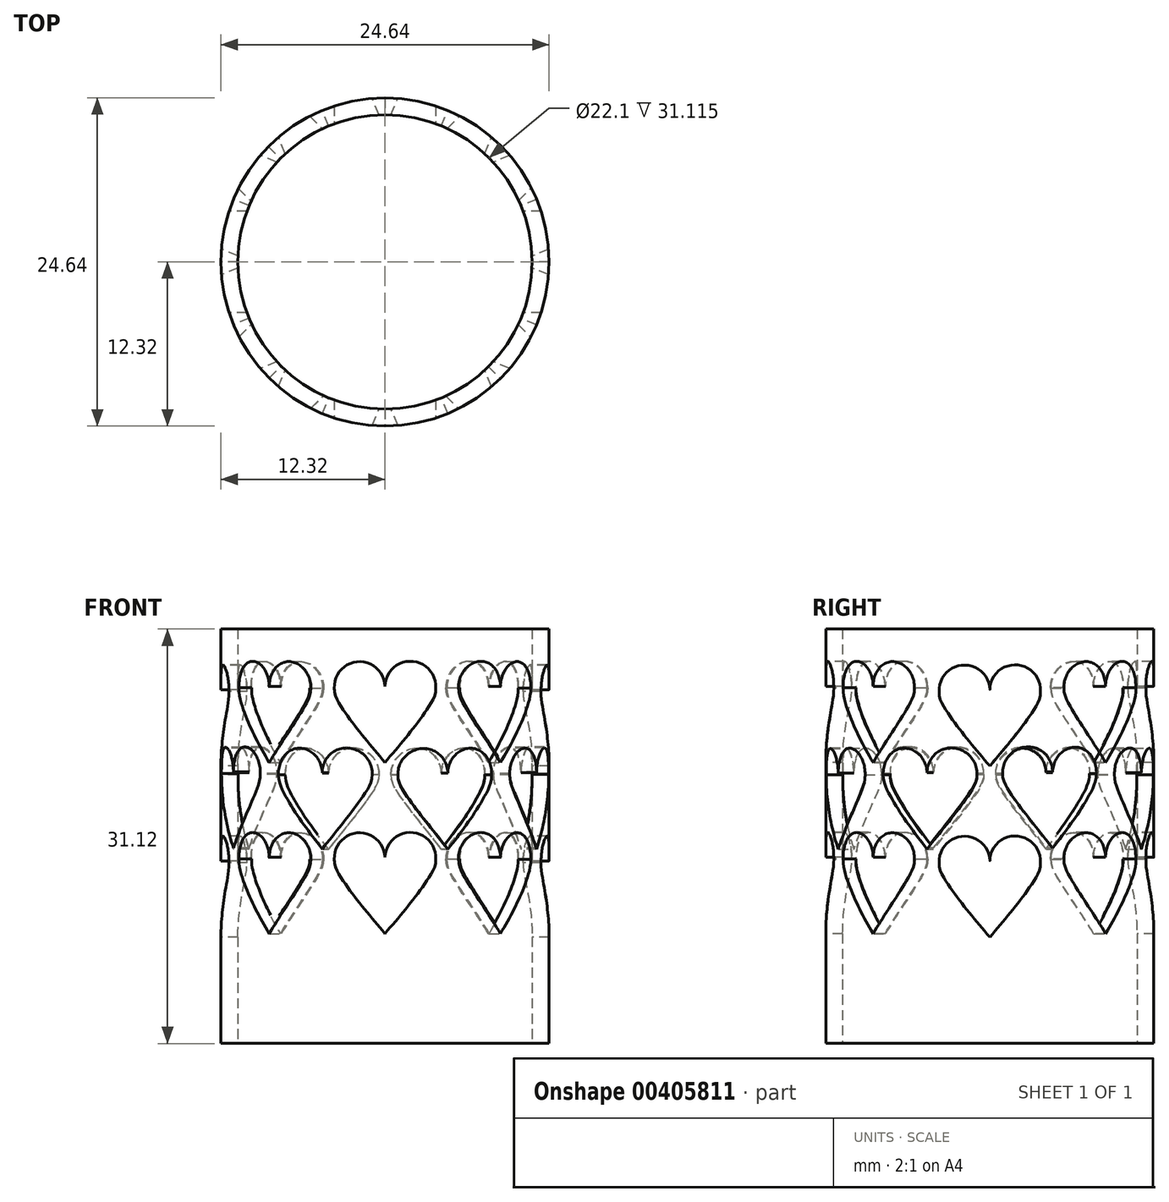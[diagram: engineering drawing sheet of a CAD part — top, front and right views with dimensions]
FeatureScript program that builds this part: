
annotation { "Feature Type Name" : "Feature", "Feature Type Description" : "" }
export const myFeature = defineFeature(function(context is Context, id is Id, definition is map)
    precondition{}
    {
        {
            var Q0;
            Q0=qCreatedBy(makeId("Top.planeOp"),FACE);
            var sketch = newSketch(context, id + "F0", { "sketchPlane" : qUnion([Q0])});
            skCircle(sketch, "E0", {"center": v(0, 0) * mm, "radius": 11.05 * mm});
            skCircle(sketch, "E1.0", {"center": v(0, 0) * mm, "radius": 12.32 * mm});
            skSolve(sketch);
        }
        {
            var Q0;
            Q0 = qSketchRegion(id + "F0", true);
            extrude(context, id + "F1", {"entities" : qUnion([Q0]), "depth" : 25.4 * mm, "hasSecondDirection" : true, "secondDirectionOppositeDirection" : true, "secondDirectionDepth" : 5.7 * mm});
        }
        {
            var Q0;
            Q0=qCreatedBy(makeId("Front.planeOp"),FACE);
            var sketch = newSketch(context, id + "F2", { "sketchPlane" : qUnion([Q0])});
            skLineSegment(sketch, "E2", {"start": v(-15.94, 0) * mm, "end": v(15.78, 0) * mm, "construction": true});
            skFitSpline(sketch, "E3.0", {"points": [v(-3.81, 8.23) * mm, v(-3.8, 8.14) * mm, v(-3.8, 8) * mm, v(-3.8, 7.85) * mm, v(-3.77, 7.7) * mm, v(-3.72, 7.54) * mm, v(-3.63, 7.32) * mm, v(-3.45, 7) * mm, v(-3.2, 6.6) * mm, v(-2.8, 6) * mm, v(-2.14, 5.12) * mm, v(-1.2, 3.96) * mm, v(-0.14, 2.7) * mm, v(0.6, 1.84) * mm, v(0.97, 1.4) * mm]});
            skArc(sketch, "E4", {"start": v(0, 8.17) * mm, "mid": v(-1.94, 10.1) * mm, "end": v(-3.8, 8.1) * mm});
            skArc(sketch, "E5", {"start": v(3.8, 8.13) * mm, "mid": v(1.93, 10.13) * mm, "end": v(0, 8.17) * mm});
            skFitSpline(sketch, "E6.0", {"points": [v(3.81, 8.23) * mm, v(3.8, 8.14) * mm, v(3.8, 8) * mm, v(3.8, 7.85) * mm, v(3.77, 7.7) * mm, v(3.72, 7.54) * mm, v(3.63, 7.32) * mm, v(3.45, 7) * mm, v(3.2, 6.6) * mm, v(2.8, 6) * mm, v(2.14, 5.12) * mm, v(1.2, 3.96) * mm, v(0.14, 2.7) * mm, v(-0.6, 1.84) * mm, v(-0.97, 1.4) * mm]});
            skFitSpline(sketch, "E7.0", {"points": [v(-3.81, 21.08) * mm, v(-3.8, 21) * mm, v(-3.8, 20.85) * mm, v(-3.8, 20.7) * mm, v(-3.77, 20.56) * mm, v(-3.72, 20.4) * mm, v(-3.63, 20.17) * mm, v(-3.45, 19.84) * mm, v(-3.2, 19.45) * mm, v(-2.8, 18.85) * mm, v(-2.14, 17.98) * mm, v(-1.2, 16.8) * mm, v(-0.14, 15.56) * mm, v(0.6, 14.7) * mm, v(0.97, 14.26) * mm]});
            skArc(sketch, "E8", {"start": v(0, 21.02) * mm, "mid": v(-1.94, 22.96) * mm, "end": v(-3.8, 20.96) * mm});
            skArc(sketch, "E9", {"start": v(3.8, 20.98) * mm, "mid": v(1.93, 22.98) * mm, "end": v(0, 21.02) * mm});
            skFitSpline(sketch, "E10.0", {"points": [v(3.81, 21.08) * mm, v(3.8, 21) * mm, v(3.8, 20.85) * mm, v(3.8, 20.7) * mm, v(3.77, 20.56) * mm, v(3.72, 20.4) * mm, v(3.63, 20.17) * mm, v(3.45, 19.84) * mm, v(3.2, 19.45) * mm, v(2.8, 18.85) * mm, v(2.14, 17.98) * mm, v(1.2, 16.8) * mm, v(0.14, 15.56) * mm, v(-0.6, 14.7) * mm, v(-0.97, 14.26) * mm]});
            skSolve(sketch);
        }
        {
            var Q0;
            Q0 = qSketchRegion(id + "F2", true);
            extrude(context, id + "F3", {"entities" : qUnion([Q0]), "operationType" : NewBodyOperationType.REMOVE, "endBound" : BoundingType.SYMMETRIC, "oppositeDirection" : true, "depth" : 50.8 * mm});
        }
        {
            var Q0;
            Q0=qCreatedBy(makeId("Right.planeOp"),FACE);
            var sketch = newSketch(context, id + "F4", { "sketchPlane" : qUnion([Q0])});
            skLineSegment(sketch, "E11", {"start": v(-15.94, -0.26) * mm, "end": v(15.78, -0.26) * mm, "construction": true});
            skFitSpline(sketch, "E12.0", {"points": [v(-3.81, 7.96) * mm, v(-3.8, 7.88) * mm, v(-3.8, 7.74) * mm, v(-3.8, 7.58) * mm, v(-3.77, 7.45) * mm, v(-3.72, 7.28) * mm, v(-3.63, 7.05) * mm, v(-3.45, 6.73) * mm, v(-3.2, 6.33) * mm, v(-2.8, 5.73) * mm, v(-2.14, 4.86) * mm, v(-1.2, 3.7) * mm, v(-0.14, 2.44) * mm, v(0.6, 1.58) * mm, v(0.97, 1.15) * mm]});
            skArc(sketch, "E13", {"start": v(0, 7.9) * mm, "mid": v(-1.94, 9.85) * mm, "end": v(-3.8, 7.84) * mm});
            skArc(sketch, "E14", {"start": v(3.8, 7.86) * mm, "mid": v(1.93, 9.87) * mm, "end": v(0, 7.9) * mm});
            skFitSpline(sketch, "E15.0", {"points": [v(3.81, 7.96) * mm, v(3.8, 7.88) * mm, v(3.8, 7.74) * mm, v(3.8, 7.58) * mm, v(3.77, 7.45) * mm, v(3.72, 7.28) * mm, v(3.63, 7.05) * mm, v(3.45, 6.73) * mm, v(3.2, 6.33) * mm, v(2.8, 5.73) * mm, v(2.14, 4.86) * mm, v(1.2, 3.7) * mm, v(0.14, 2.44) * mm, v(-0.6, 1.58) * mm, v(-0.97, 1.15) * mm]});
            skFitSpline(sketch, "E16.0", {"points": [v(-3.81, 20.82) * mm, v(-3.8, 20.73) * mm, v(-3.8, 20.6) * mm, v(-3.8, 20.44) * mm, v(-3.77, 20.3) * mm, v(-3.72, 20.13) * mm, v(-3.63, 19.9) * mm, v(-3.45, 19.58) * mm, v(-3.2, 19.19) * mm, v(-2.8, 18.58) * mm, v(-2.14, 17.72) * mm, v(-1.2, 16.55) * mm, v(-0.14, 15.3) * mm, v(0.6, 14.43) * mm, v(0.97, 14) * mm]});
            skArc(sketch, "E17", {"start": v(0, 20.76) * mm, "mid": v(-1.94, 22.7) * mm, "end": v(-3.8, 20.7) * mm});
            skArc(sketch, "E18", {"start": v(3.8, 20.72) * mm, "mid": v(1.93, 22.72) * mm, "end": v(0, 20.76) * mm});
            skFitSpline(sketch, "E19.0", {"points": [v(3.81, 20.82) * mm, v(3.8, 20.73) * mm, v(3.8, 20.6) * mm, v(3.8, 20.44) * mm, v(3.77, 20.3) * mm, v(3.72, 20.13) * mm, v(3.63, 19.9) * mm, v(3.45, 19.58) * mm, v(3.2, 19.19) * mm, v(2.8, 18.58) * mm, v(2.14, 17.72) * mm, v(1.2, 16.55) * mm, v(0.14, 15.3) * mm, v(-0.6, 14.43) * mm, v(-0.97, 14) * mm]});
            skSolve(sketch);
        }
        {
            var Q0;
            Q0 = qSketchRegion(id + "F4", true);
            extrude(context, id + "F5", {"entities" : qUnion([Q0]), "operationType" : NewBodyOperationType.REMOVE, "endBound" : BoundingType.SYMMETRIC, "depth" : 50.8 * mm});
        }
        {
            var Q0;
            Q0=qCreatedBy(makeId("Top.planeOp"),FACE);
            var sketch = newSketch(context, id + "F6", { "sketchPlane" : qUnion([Q0])});
            skLineSegment(sketch, "E20", {"start": v(-35.33, -35.33) * mm, "end": v(35.33, 35.33) * mm, "construction": true});
            skLineSegment(sketch, "E21.MirrorCS", {"start": v(35.33, -35.33) * mm, "end": v(-35.33, 35.33) * mm, "construction": true});
            skLineSegment(sketch, "E22", {"start": v(0, 0) * mm, "end": v(25.2, 60.83) * mm, "construction": true});
            skLineSegment(sketch, "E23.1.0", {"start": v(0, 0) * mm, "end": v(-25.2, 60.83) * mm, "construction": true});
            skLineSegment(sketch, "E23.2.0", {"start": v(0, 0) * mm, "end": v(-60.83, 25.2) * mm, "construction": true});
            skLineSegment(sketch, "E23.3.0", {"start": v(0, 0) * mm, "end": v(-60.83, -25.2) * mm, "construction": true});
            skLineSegment(sketch, "E23.4.0", {"start": v(0, 0) * mm, "end": v(-25.2, -60.83) * mm, "construction": true});
            skLineSegment(sketch, "E23.5.0", {"start": v(0, 0) * mm, "end": v(25.2, -60.83) * mm, "construction": true});
            skLineSegment(sketch, "E23.6.0", {"start": v(0, 0) * mm, "end": v(60.83, -25.2) * mm, "construction": true});
            skLineSegment(sketch, "E23.7.0", {"start": v(0, 0) * mm, "end": v(60.83, 25.2) * mm, "construction": true});
            skPoint(sketch, "E23.center", {"position": v(0, 0) * mm});
            skSolve(sketch);
        }
        {
            var Q0;
            Q0=sQuery(id+"F6.wireOp",EDGE,"E21.MirrorCS");
            cPlane(context, id + "F7", {"entities" : qUnion([Q0]), "cplaneType" : CPlaneType.MID_PLANE, "offset" : 25.4 * mm, "width" : 152.4 * mm, "height" : 152.4 * mm});
        }
        {
            var Q0;
            Q0=sQuery(id+"F6.wireOp",EDGE,"E20");
            cPlane(context, id + "F8", {"entities" : qUnion([Q0]), "cplaneType" : CPlaneType.MID_PLANE, "offset" : 25.4 * mm, "width" : 152.4 * mm, "height" : 152.4 * mm});
        }
        {
            var Q0;
            Q0=qCreatedBy(id+"F7.planeOp",FACE);
            var sketch = newSketch(context, id + "F9", { "sketchPlane" : qUnion([Q0])});
            skLineSegment(sketch, "E24", {"start": v(-15.87, 0) * mm, "end": v(15.85, 0) * mm, "construction": true});
            skFitSpline(sketch, "E25.0", {"points": [v(-3.74, 8.23) * mm, v(-3.74, 8.14) * mm, v(-3.73, 8) * mm, v(-3.72, 7.85) * mm, v(-3.7, 7.7) * mm, v(-3.65, 7.54) * mm, v(-3.56, 7.32) * mm, v(-3.38, 7) * mm, v(-3.13, 6.6) * mm, v(-2.72, 6) * mm, v(-2.07, 5.12) * mm, v(-1.12, 3.96) * mm, v(-0.07, 2.7) * mm, v(0.67, 1.84) * mm, v(1.04, 1.4) * mm]});
            skArc(sketch, "E26", {"start": v(0.07, 8.17) * mm, "mid": v(-1.86, 10.1) * mm, "end": v(-3.74, 8.1) * mm});
            skArc(sketch, "E27", {"start": v(3.88, 8.13) * mm, "mid": v(2, 10.13) * mm, "end": v(0.07, 8.17) * mm});
            skFitSpline(sketch, "E28.0", {"points": [v(3.88, 8.23) * mm, v(3.88, 8.14) * mm, v(3.88, 8) * mm, v(3.87, 7.85) * mm, v(3.84, 7.7) * mm, v(3.8, 7.54) * mm, v(3.7, 7.32) * mm, v(3.52, 7) * mm, v(3.28, 6.6) * mm, v(2.87, 6) * mm, v(2.21, 5.12) * mm, v(1.27, 3.96) * mm, v(0.22, 2.7) * mm, v(-0.52, 1.84) * mm, v(-0.9, 1.4) * mm]});
            skFitSpline(sketch, "E29.0", {"points": [v(-3.74, 21.08) * mm, v(-3.74, 21) * mm, v(-3.73, 20.85) * mm, v(-3.72, 20.7) * mm, v(-3.7, 20.56) * mm, v(-3.65, 20.4) * mm, v(-3.56, 20.17) * mm, v(-3.38, 19.84) * mm, v(-3.13, 19.45) * mm, v(-2.72, 18.85) * mm, v(-2.07, 17.98) * mm, v(-1.12, 16.8) * mm, v(-0.07, 15.56) * mm, v(0.67, 14.7) * mm, v(1.04, 14.26) * mm]});
            skArc(sketch, "E30", {"start": v(0.07, 21.02) * mm, "mid": v(-1.86, 22.96) * mm, "end": v(-3.74, 20.96) * mm});
            skArc(sketch, "E31", {"start": v(3.88, 20.98) * mm, "mid": v(2, 22.98) * mm, "end": v(0.07, 21.02) * mm});
            skFitSpline(sketch, "E32.0", {"points": [v(3.88, 21.08) * mm, v(3.88, 21) * mm, v(3.88, 20.85) * mm, v(3.87, 20.7) * mm, v(3.84, 20.56) * mm, v(3.8, 20.4) * mm, v(3.7, 20.17) * mm, v(3.52, 19.84) * mm, v(3.28, 19.45) * mm, v(2.87, 18.85) * mm, v(2.21, 17.98) * mm, v(1.27, 16.8) * mm, v(0.22, 15.56) * mm, v(-0.52, 14.7) * mm, v(-0.9, 14.26) * mm]});
            skSolve(sketch);
        }
        {
            var Q0;
            Q0 = qSketchRegion(id + "F9", true);
            extrude(context, id + "F10", {"entities" : qUnion([Q0]), "operationType" : NewBodyOperationType.REMOVE, "endBound" : BoundingType.SYMMETRIC, "depth" : 50.8 * mm});
        }
        {
            var Q0;
            Q0=qCreatedBy(id+"F8.planeOp",FACE);
            var sketch = newSketch(context, id + "F11", { "sketchPlane" : qUnion([Q0])});
            skLineSegment(sketch, "E33", {"start": v(-15.96, 0) * mm, "end": v(15.75, 0) * mm, "construction": true});
            skFitSpline(sketch, "E34.0", {"points": [v(-3.83, 8.23) * mm, v(-3.83, 8.14) * mm, v(-3.83, 8) * mm, v(-3.82, 7.85) * mm, v(-3.8, 7.7) * mm, v(-3.75, 7.54) * mm, v(-3.65, 7.32) * mm, v(-3.48, 7) * mm, v(-3.23, 6.6) * mm, v(-2.82, 6) * mm, v(-2.16, 5.12) * mm, v(-1.22, 3.96) * mm, v(-0.17, 2.7) * mm, v(0.57, 1.84) * mm, v(0.94, 1.4) * mm]});
            skArc(sketch, "E35", {"start": v(-0.02, 8.17) * mm, "mid": v(-1.96, 10.1) * mm, "end": v(-3.83, 8.1) * mm});
            skArc(sketch, "E36", {"start": v(3.78, 8.13) * mm, "mid": v(1.9, 10.13) * mm, "end": v(-0.02, 8.17) * mm});
            skFitSpline(sketch, "E37.0", {"points": [v(3.79, 8.23) * mm, v(3.78, 8.14) * mm, v(3.78, 8) * mm, v(3.77, 7.85) * mm, v(3.75, 7.7) * mm, v(3.7, 7.54) * mm, v(3.6, 7.32) * mm, v(3.43, 7) * mm, v(3.18, 6.6) * mm, v(2.77, 6) * mm, v(2.12, 5.12) * mm, v(1.17, 3.96) * mm, v(0.12, 2.7) * mm, v(-0.62, 1.84) * mm, v(-0.99, 1.4) * mm]});
            skFitSpline(sketch, "E38.0", {"points": [v(-3.83, 21.08) * mm, v(-3.83, 21) * mm, v(-3.83, 20.85) * mm, v(-3.82, 20.7) * mm, v(-3.8, 20.56) * mm, v(-3.75, 20.4) * mm, v(-3.65, 20.17) * mm, v(-3.48, 19.84) * mm, v(-3.23, 19.45) * mm, v(-2.82, 18.85) * mm, v(-2.16, 17.98) * mm, v(-1.22, 16.8) * mm, v(-0.17, 15.56) * mm, v(0.57, 14.7) * mm, v(0.94, 14.26) * mm]});
            skArc(sketch, "E39", {"start": v(-0.02, 21.02) * mm, "mid": v(-1.96, 22.96) * mm, "end": v(-3.83, 20.96) * mm});
            skArc(sketch, "E40", {"start": v(3.78, 20.98) * mm, "mid": v(1.9, 22.98) * mm, "end": v(-0.02, 21.02) * mm});
            skFitSpline(sketch, "E41.0", {"points": [v(3.79, 21.08) * mm, v(3.78, 21) * mm, v(3.78, 20.85) * mm, v(3.77, 20.7) * mm, v(3.75, 20.56) * mm, v(3.7, 20.4) * mm, v(3.6, 20.17) * mm, v(3.43, 19.84) * mm, v(3.18, 19.45) * mm, v(2.77, 18.85) * mm, v(2.12, 17.98) * mm, v(1.17, 16.8) * mm, v(0.12, 15.56) * mm, v(-0.62, 14.7) * mm, v(-0.99, 14.26) * mm]});
            skSolve(sketch);
        }
        {
            var Q0;
            Q0 = qSketchRegion(id + "F11", true);
            extrude(context, id + "F12", {"entities" : qUnion([Q0]), "operationType" : NewBodyOperationType.REMOVE, "endBound" : BoundingType.SYMMETRIC, "oppositeDirection" : true, "depth" : 50.8 * mm});
        }
        {
            var Q0;
            Q0=sQuery(id+"F6.wireOp",VERTEX,"E23.2.0.end");
            var Q1;
            Q1=sQuery(id+"F6.wireOp",VERTEX,"E23.6.0.end");
            cPlane(context, id + "F13", {"entities" : qUnion([Q0, Q1]), "cplaneType" : CPlaneType.MID_PLANE, "offset" : 25.4 * mm, "width" : 152.4 * mm, "height" : 152.4 * mm});
        }
        {
            var Q0;
            Q0=qCreatedBy(id+"F13.planeOp",FACE);
            var sketch = newSketch(context, id + "F14", { "sketchPlane" : qUnion([Q0])});
            skFitSpline(sketch, "E42.0", {"points": [v(-3.81, 14.58) * mm, v(-3.8, 14.5) * mm, v(-3.8, 14.35) * mm, v(-3.8, 14.2) * mm, v(-3.77, 14.06) * mm, v(-3.72, 13.9) * mm, v(-3.63, 13.67) * mm, v(-3.45, 13.34) * mm, v(-3.2, 12.95) * mm, v(-2.8, 12.34) * mm, v(-2.14, 11.47) * mm, v(-1.2, 10.3) * mm, v(-0.14, 9.06) * mm, v(0.6, 8.2) * mm, v(0.97, 7.76) * mm]});
            skArc(sketch, "E43", {"start": v(0, 14.52) * mm, "mid": v(-1.94, 16.46) * mm, "end": v(-3.8, 14.45) * mm});
            skArc(sketch, "E44", {"start": v(3.8, 14.48) * mm, "mid": v(1.93, 16.48) * mm, "end": v(0, 14.52) * mm});
            skFitSpline(sketch, "E45.0", {"points": [v(3.81, 14.58) * mm, v(3.8, 14.5) * mm, v(3.8, 14.35) * mm, v(3.8, 14.2) * mm, v(3.77, 14.06) * mm, v(3.72, 13.9) * mm, v(3.63, 13.67) * mm, v(3.45, 13.34) * mm, v(3.2, 12.95) * mm, v(2.8, 12.34) * mm, v(2.14, 11.47) * mm, v(1.2, 10.3) * mm, v(0.14, 9.06) * mm, v(-0.6, 8.2) * mm, v(-0.97, 7.76) * mm]});
            skSolve(sketch);
        }
        {
            var Q0;
            Q0 = qSketchRegion(id + "F14", true);
            extrude(context, id + "F15", {"entities" : qUnion([Q0]), "operationType" : NewBodyOperationType.REMOVE, "endBound" : BoundingType.SYMMETRIC, "depth" : 50.8 * mm});
        }
        {
            var Q0;
            Q0=sQuery(id+"F6.wireOp",VERTEX,"E23.1.0.end");
            var Q1;
            Q1=sQuery(id+"F6.wireOp",VERTEX,"E23.5.0.end");
            cPlane(context, id + "F16", {"entities" : qUnion([Q0, Q1]), "cplaneType" : CPlaneType.MID_PLANE, "offset" : 25.4 * mm, "width" : 152.4 * mm, "height" : 152.4 * mm});
        }
        {
            var Q0;
            Q0=qCreatedBy(id+"F16.planeOp",FACE);
            var sketch = newSketch(context, id + "F17", { "sketchPlane" : qUnion([Q0])});
            skFitSpline(sketch, "E46.0", {"points": [v(-3.81, 14.55) * mm, v(-3.8, 14.47) * mm, v(-3.8, 14.33) * mm, v(-3.8, 14.17) * mm, v(-3.77, 14.03) * mm, v(-3.72, 13.87) * mm, v(-3.63, 13.64) * mm, v(-3.45, 13.32) * mm, v(-3.2, 12.92) * mm, v(-2.8, 12.32) * mm, v(-2.14, 11.45) * mm, v(-1.2, 10.28) * mm, v(-0.14, 9.03) * mm, v(0.6, 8.17) * mm, v(0.97, 7.73) * mm]});
            skArc(sketch, "E47", {"start": v(0, 14.5) * mm, "mid": v(-1.94, 16.43) * mm, "end": v(-3.8, 14.43) * mm});
            skArc(sketch, "E48", {"start": v(3.8, 14.45) * mm, "mid": v(1.93, 16.46) * mm, "end": v(0, 14.5) * mm});
            skFitSpline(sketch, "E49.0", {"points": [v(3.81, 14.55) * mm, v(3.8, 14.47) * mm, v(3.8, 14.33) * mm, v(3.8, 14.17) * mm, v(3.77, 14.03) * mm, v(3.72, 13.87) * mm, v(3.63, 13.64) * mm, v(3.45, 13.32) * mm, v(3.2, 12.92) * mm, v(2.8, 12.32) * mm, v(2.14, 11.45) * mm, v(1.2, 10.28) * mm, v(0.14, 9.03) * mm, v(-0.6, 8.17) * mm, v(-0.97, 7.73) * mm]});
            skSolve(sketch);
        }
        {
            var Q0;
            Q0 = qSketchRegion(id + "F17", true);
            extrude(context, id + "F18", {"entities" : qUnion([Q0]), "operationType" : NewBodyOperationType.REMOVE, "endBound" : BoundingType.SYMMETRIC, "depth" : 50.8 * mm});
        }
        {
            var Q0;
            Q0=sQuery(id+"F6.wireOp",VERTEX,"E22.end");
            var Q1;
            Q1=sQuery(id+"F6.wireOp",VERTEX,"E23.4.0.end");
            cPlane(context, id + "F19", {"entities" : qUnion([Q0, Q1]), "cplaneType" : CPlaneType.MID_PLANE, "offset" : 25.4 * mm, "width" : 152.4 * mm, "height" : 152.4 * mm});
        }
        {
            var Q0;
            Q0=qCreatedBy(id+"F19.planeOp",FACE);
            var sketch = newSketch(context, id + "F20", { "sketchPlane" : qUnion([Q0])});
            skFitSpline(sketch, "E50.0", {"points": [v(-3.81, 14.58) * mm, v(-3.8, 14.5) * mm, v(-3.8, 14.35) * mm, v(-3.8, 14.2) * mm, v(-3.77, 14.06) * mm, v(-3.72, 13.9) * mm, v(-3.63, 13.67) * mm, v(-3.45, 13.34) * mm, v(-3.2, 12.95) * mm, v(-2.8, 12.34) * mm, v(-2.14, 11.47) * mm, v(-1.2, 10.3) * mm, v(-0.14, 9.06) * mm, v(0.6, 8.2) * mm, v(0.97, 7.76) * mm]});
            skArc(sketch, "E51", {"start": v(0, 14.52) * mm, "mid": v(-1.94, 16.46) * mm, "end": v(-3.8, 14.45) * mm});
            skArc(sketch, "E52", {"start": v(3.8, 14.48) * mm, "mid": v(1.93, 16.48) * mm, "end": v(0, 14.52) * mm});
            skFitSpline(sketch, "E53.0", {"points": [v(3.81, 14.58) * mm, v(3.8, 14.5) * mm, v(3.8, 14.35) * mm, v(3.8, 14.2) * mm, v(3.77, 14.06) * mm, v(3.72, 13.9) * mm, v(3.63, 13.67) * mm, v(3.45, 13.34) * mm, v(3.2, 12.95) * mm, v(2.8, 12.34) * mm, v(2.14, 11.47) * mm, v(1.2, 10.3) * mm, v(0.14, 9.06) * mm, v(-0.6, 8.2) * mm, v(-0.97, 7.76) * mm]});
            skSolve(sketch);
        }
        {
            var Q0;
            Q0 = qSketchRegion(id + "F20", true);
            extrude(context, id + "F21", {"entities" : qUnion([Q0]), "operationType" : NewBodyOperationType.REMOVE, "endBound" : BoundingType.SYMMETRIC, "depth" : 50.8 * mm});
        }
        {
            var Q0;
            Q0=sQuery(id+"F6.wireOp",VERTEX,"E23.7.0.end");
            var Q1;
            Q1=sQuery(id+"F6.wireOp",VERTEX,"E23.3.0.end");
            cPlane(context, id + "F22", {"entities" : qUnion([Q0, Q1]), "cplaneType" : CPlaneType.MID_PLANE, "offset" : 25.4 * mm, "width" : 152.4 * mm, "height" : 152.4 * mm});
        }
        {
            var Q0;
            Q0=qCreatedBy(id+"F22.planeOp",FACE);
            var sketch = newSketch(context, id + "F23", { "sketchPlane" : qUnion([Q0])});
            skFitSpline(sketch, "E54.0", {"points": [v(-3.81, 14.65) * mm, v(-3.8, 14.57) * mm, v(-3.8, 14.43) * mm, v(-3.8, 14.27) * mm, v(-3.77, 14.14) * mm, v(-3.72, 13.97) * mm, v(-3.63, 13.74) * mm, v(-3.45, 13.42) * mm, v(-3.2, 13.02) * mm, v(-2.8, 12.42) * mm, v(-2.14, 11.55) * mm, v(-1.2, 10.38) * mm, v(-0.14, 9.13) * mm, v(0.6, 8.27) * mm, v(0.97, 7.84) * mm]});
            skArc(sketch, "E55", {"start": v(0, 14.6) * mm, "mid": v(-1.94, 16.54) * mm, "end": v(-3.8, 14.53) * mm});
            skArc(sketch, "E56", {"start": v(3.8, 14.55) * mm, "mid": v(1.93, 16.56) * mm, "end": v(0, 14.6) * mm});
            skFitSpline(sketch, "E57.0", {"points": [v(3.81, 14.65) * mm, v(3.8, 14.57) * mm, v(3.8, 14.43) * mm, v(3.8, 14.27) * mm, v(3.77, 14.14) * mm, v(3.72, 13.97) * mm, v(3.63, 13.74) * mm, v(3.45, 13.42) * mm, v(3.2, 13.02) * mm, v(2.8, 12.42) * mm, v(2.14, 11.55) * mm, v(1.2, 10.38) * mm, v(0.14, 9.13) * mm, v(-0.6, 8.27) * mm, v(-0.97, 7.84) * mm]});
            skSolve(sketch);
        }
        {
            var Q0;
            Q0 = qSketchRegion(id + "F23", true);
            extrude(context, id + "F24", {"entities" : qUnion([Q0]), "operationType" : NewBodyOperationType.REMOVE, "endBound" : BoundingType.SYMMETRIC, "oppositeDirection" : true, "depth" : 50.8 * mm});
        }
    });
